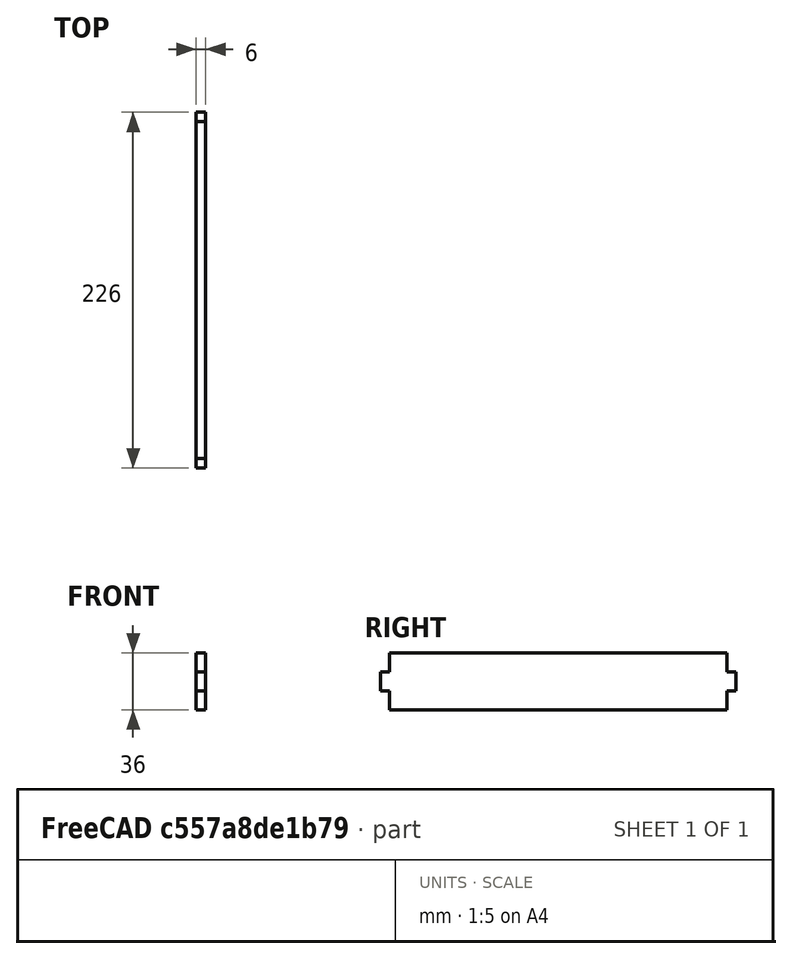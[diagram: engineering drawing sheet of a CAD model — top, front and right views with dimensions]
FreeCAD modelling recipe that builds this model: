
FCSTD DOCUMENT  (FreeCAD 0.16RUnknown)
Label: BASE_JUPE_FEMELLE
License: All rights reserved
LicenseURL: http://en.wikipedia.org/wiki/All_rights_reserved
objects: Spreadsheet::Sheet×1, Sketcher::SketchObject×1, PartDesign::Pad×1
note: 3 computed .brp shape members not serialized (recipe doc carries the construction recipe); baked Part::Feature solids carry a one-line shape summary decoded from their .brp

FEATURE [Spreadsheet::Sheet] Spreadsheet  label="prefs"
  cells = A1=PCBHeated; B1(pcbheated)=214; C1=mm; D1=name=pcbheated; A2=Plexi thickness; B2(plexi)=6; C2=mm; D2=name=plexi
FEATURE [Sketcher::SketchObject] Sketch
  Placement = pos=(0,0,0) rot=(0.57735,0.57735,0.57735;2.0944rad)
  expr: Constraints[34] = prefs.pcbheated
  expr: Constraints[20] = prefs.pcbheated
  expr: Constraints[25] = prefs.plexi * 2
  expr: Constraints[28] = prefs.plexi
  sketch-geometry (12):
    g0: LineSegment StartX=0 StartY=0 StartZ=0 EndX=214 EndY=0 EndZ=0
    g1: LineSegment StartX=214 StartY=0 StartZ=0 EndX=214 EndY=12 EndZ=0
    g2: LineSegment StartX=214 StartY=12 StartZ=0 EndX=220 EndY=12 EndZ=0
    g3: LineSegment StartX=220 StartY=12 StartZ=0 EndX=220 EndY=24 EndZ=0
    g4: LineSegment StartX=220 StartY=24 StartZ=0 EndX=214 EndY=24 EndZ=0
    g5: LineSegment StartX=214 StartY=24 StartZ=0 EndX=214 EndY=36 EndZ=0
    g6: LineSegment StartX=214 StartY=36 StartZ=0 EndX=0 EndY=36 EndZ=0
    g7: LineSegment StartX=0 StartY=36 StartZ=0 EndX=0 EndY=24 EndZ=0
    g8: LineSegment StartX=0 StartY=24 StartZ=0 EndX=-6 EndY=24 EndZ=0
    g9: LineSegment StartX=-6 StartY=24 StartZ=0 EndX=-6 EndY=12 EndZ=0
    g10: LineSegment StartX=-6 StartY=12 StartZ=0 EndX=0 EndY=12 EndZ=0
    g11: LineSegment StartX=0 StartY=12 StartZ=0 EndX=0 EndY=0 EndZ=0
  constraints (35):
    c: Coincident(g0,g-1)
    c: Horizontal(g0)
    c: Coincident(g1,g0)
    c: Vertical(g1)
    c: Horizontal(g2)
    c: Coincident(g3,g2)
    c: Vertical(g3)
    c: Horizontal(g4)
    c: Vertical(g5)
    c: Horizontal(g6)
    c: Coincident(g7,g6)
    c: Vertical(g7)
    c: Horizontal(g8)
    c: Horizontal(g10)
    c: Coincident(g11,g10)
    c: Coincident(g11,g-1)
    c: Vertical(g11)
    c: Coincident(g9,g8)
    c: Vertical(g9)
    c: Coincident(g10,g9)
    c: DistanceX(g0,g0) = 214
    c: Coincident(g2,g1)
    c: Coincident(g4,g3)
    c: Coincident(g5,g4)
    c: Coincident(g6,g5)
    c: DistanceY(g1,g1) = 12
    c: Equal(g5,g1)
    c: Equal(g3,g1)
    c: DistanceX(g4,g4) = 6
    c: Equal(g2,g4)
    c: Coincident(g7,g8)
    c: Equal(g7,g1)
    c: Equal(g9,g1)
    c: Equal(g10,g4)
    c: DistanceX(g6,g6) = 214
FEATURE [PartDesign::Pad] Pad
  Length = 6
  Length2 = 100
  Placement = pos=(0,0,0) rot=(0.57735,0.57735,0.57735;2.0944rad)
  Sketch = -> Sketch
  Type = 0
